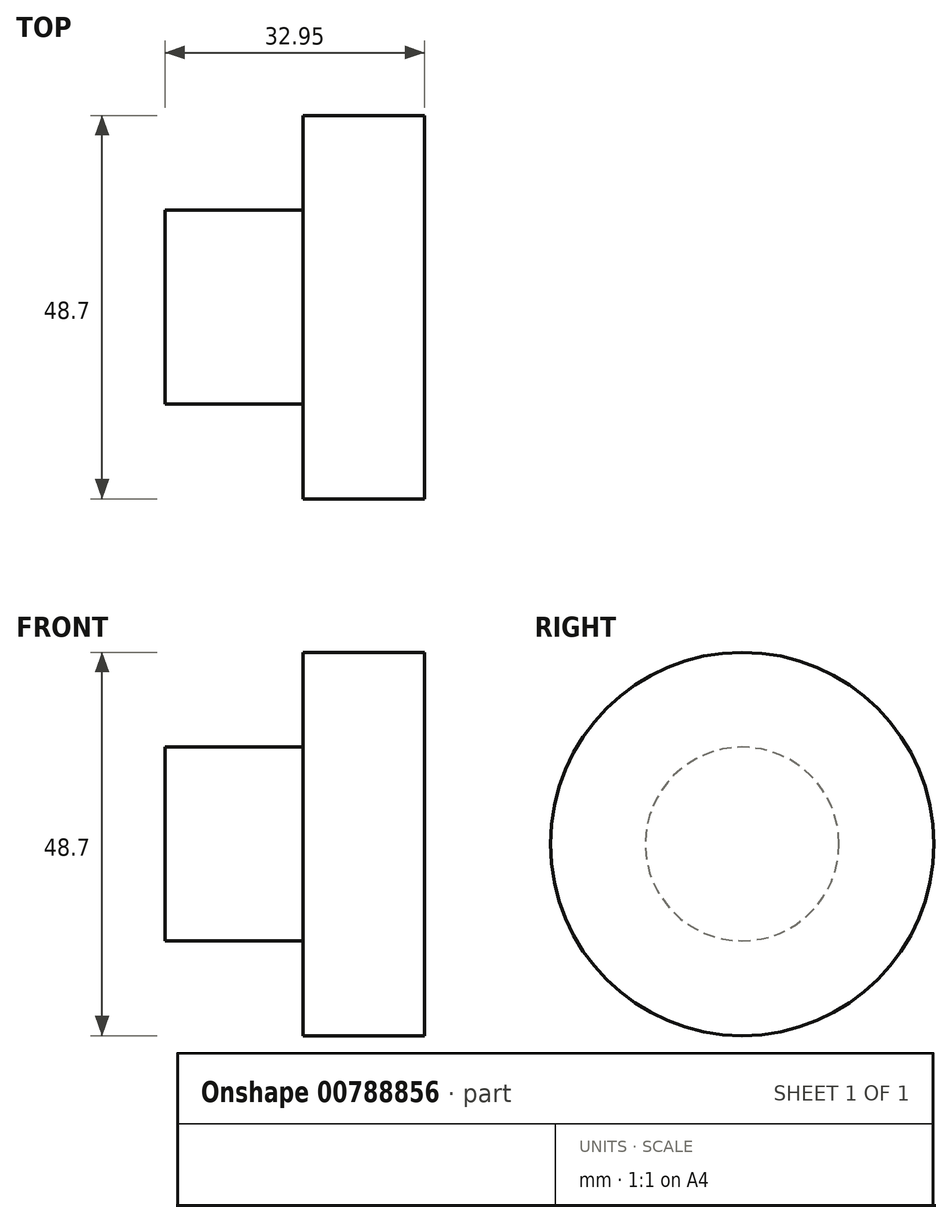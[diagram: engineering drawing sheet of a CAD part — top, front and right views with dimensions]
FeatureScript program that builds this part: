
annotation { "Feature Type Name" : "Feature", "Feature Type Description" : "" }
export const myFeature = defineFeature(function(context is Context, id is Id, definition is map)
    precondition{}
    {
        {
            var Q0;
            Q0=qCreatedBy(makeId("Front.planeOp"),FACE);
            var sketch = newSketch(context, id + "F0", { "sketchPlane" : qUnion([Q0])});
            skLineSegment(sketch, "E0", {"start": v(0, 0) * mm, "end": v(32.95, 0) * mm});
            skLineSegment(sketch, "E1", {"start": v(32.95, 0) * mm, "end": v(32.95, 24.35) * mm});
            skLineSegment(sketch, "E2", {"start": v(32.95, 24.35) * mm, "end": v(17.5, 24.35) * mm});
            skLineSegment(sketch, "E3", {"start": v(17.5, 24.35) * mm, "end": v(17.5, 12.3) * mm});
            skLineSegment(sketch, "E4", {"start": v(17.5, 12.3) * mm, "end": v(0, 12.3) * mm});
            skLineSegment(sketch, "E5", {"start": v(0, 12.3) * mm, "end": v(0, 0) * mm});
            skSolve(sketch);
        }
        {
            var Q0;
            Q0 = qSketchRegion(id + "F0", true);
            var Q1;
            Q1=sQuery(id+"F0.wireOp",EDGE,"E0");
            revolve(context, id + "F1", {"surfaceOperationType" : NewSurfaceOperationType.NEW, "entities" : qUnion([Q0]), "axis" : qUnion([Q1]), "revolveType" : RevolveType.FULL});
        }
    });
